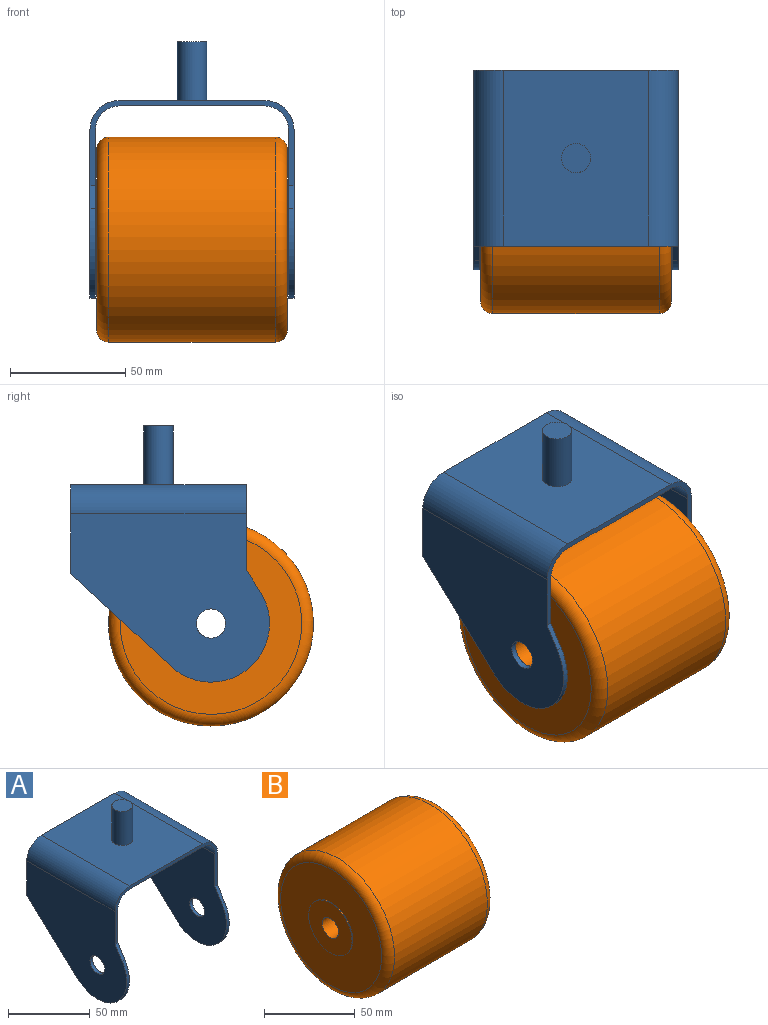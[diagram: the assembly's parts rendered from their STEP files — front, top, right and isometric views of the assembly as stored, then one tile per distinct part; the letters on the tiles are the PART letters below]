
ASSEMBLY  parts=2 mates=1
PART A: 22 faces, bbox 88.5x86.3x111.1 mm
  f0: plane 86.31x73.03mm, normal (-1,0,0), area 4493.5mm2, adj f3,f6,f7,f8,f9,f10,f11
  f1: plane 86.31x73.03mm, normal (1,0,0), area 4493.5mm2, adj f4,f6,f7,f8,f9,f10,f11
  f2: plane 76.2x63.11mm, normal (0,0,1), area 4682mm2, adj f4,f6,f9,f15,f20
  f3: cylinder r=10.34mm len=76.2mm, axis (0,1,0), area 1237.4mm2, adj f0,f5,f6,f9
  f4: cylinder r=12.7mm len=76.2mm, axis (0,1,0), area 1520.1mm2, adj f1,f2,f6,f9
  f5: plane 76.2x63.11mm, normal (0,0,-1), area 4808.7mm2, adj f3,f6,f9,f14
  f6: plane 88.51x36.95mm, normal (0,-1,0), area 349.1mm2, adj f0,f1,f2,f3,f4,f5,f8,f12
  f7: cylinder r=25.4mm len=42.65mm, axis (-1,0,0), area 172.8mm2, adj f0,f1,f8,f10
  f8: plane 9.83x6.2mm, normal (0,-0.85,0.53), area 27.4mm2, adj f0,f1,f6,f7
  f9: plane 88.51x38.59mm, normal (0,1,0), area 356.9mm2, adj f0,f1,f2,f3,f4,f5,f10,f12
  f10: plane 43.66x40.38mm, normal (0,0.68,-0.73), area 140.5mm2, adj f0,f1,f7,f9
  f11: cylinder r=6.35mm len=12.7mm, axis (-1,0,0), area 94.2mm2, adj f0,f1
  f12: plane 86.31x73.03mm, normal (1,0,0), area 4493.5mm2, adj f6,f9,f14,f16,f17,f18,f19
  f13: plane 86.31x73.03mm, normal (-1,0,0), area 4493.5mm2, adj f6,f9,f15,f16,f17,f18,f19
  f14: cylinder r=10.34mm len=76.2mm, axis (0,1,0), area 1237.4mm2, adj f5,f6,f9,f12
  f15: cylinder r=12.7mm len=76.2mm, axis (0,1,0), area 1520.1mm2, adj f2,f6,f9,f13
  f16: cylinder r=25.4mm len=42.65mm, axis (1,0,0), area 172.8mm2, adj f12,f13,f17,f18
  f17: plane 9.83x6.2mm, normal (0,-0.85,0.53), area 27.4mm2, adj f6,f12,f13,f16
  f18: plane 43.66x40.38mm, normal (0,0.68,-0.73), area 140.5mm2, adj f9,f12,f13,f16
  f19: cylinder r=6.35mm len=12.7mm, axis (1,0,0), area 94.2mm2, adj f12,f13
  f20: cylinder r=6.35mm len=25.4mm, axis (0,0,-1), area 1013.4mm2, adj f2,f21
  f21: plane 12.7x12.7mm, normal (0,0,1), area 126.7mm2, adj f20
PART B: 10 faces, bbox 83.7x96.2x96.2 mm
  f0: cylinder r=44.45mm len=88.9mm, axis (-1,0,0), area 20217.6mm2, adj f5,f9
  f1: plane 78.74x78.74mm, normal (1,0,0), area 3968.6mm2, adj f2,f5
  f2: cylinder r=16.93mm len=33.87mm, axis (-1,0,0), area 62.8mm2, adj f1,f3
  f3: plane 33.87x33.87mm, normal (1,0,0), area 774.1mm2, adj f2,f4
  f4: cylinder r=6.35mm len=83.73mm, axis (-1,0,0), area 3340.7mm2, adj f3,f8
  f5: torus R=39.37mm, axis (1,0,0), area 2136.1mm2, adj f0,f1
  f6: plane 78.74x78.74mm, normal (-1,0,0), area 3968.6mm2, adj f7,f9
  f7: cylinder r=16.93mm len=33.87mm, axis (1,0,0), area 62.8mm2, adj f6,f8
  f8: plane 33.87x33.87mm, normal (-1,0,0), area 774.1mm2, adj f4,f7
  f9: torus R=39.37mm, axis (-1,0,0), area 2136.1mm2, adj f0,f6
PLACE A at identity fixed
PLACE B rot(axis=(-1,0,0),41.9deg) t=(0,-29.69,11.37)mm
MATE revolute B.f0 <-> A.f7  axis (-1,0,0) through (0,0,44.45)mm
